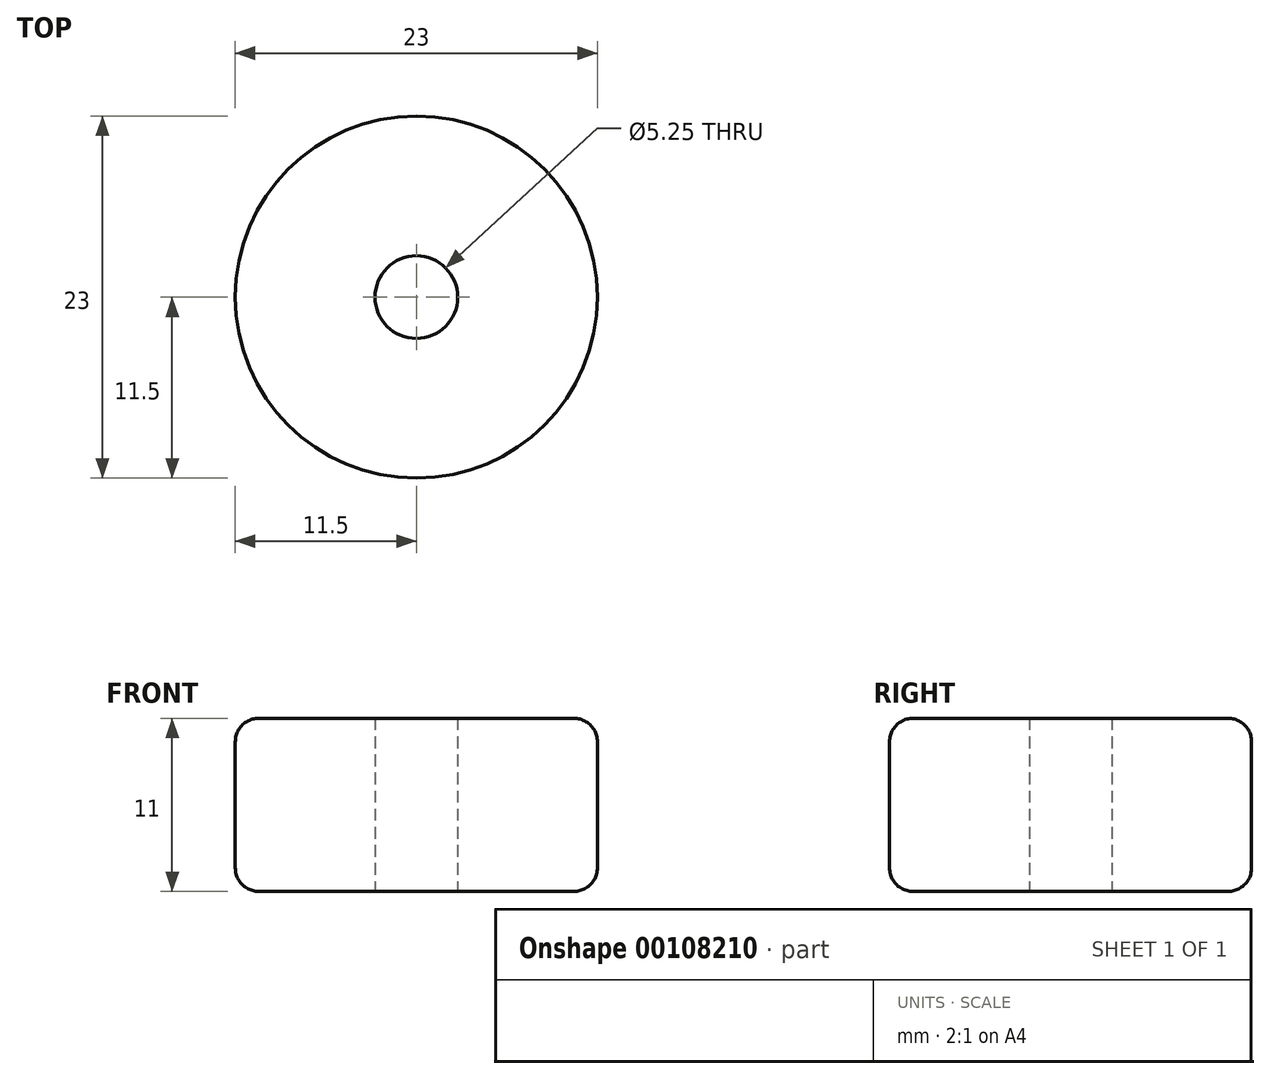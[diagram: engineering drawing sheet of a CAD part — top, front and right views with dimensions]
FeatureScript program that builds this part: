
annotation { "Feature Type Name" : "Feature", "Feature Type Description" : "" }
export const myFeature = defineFeature(function(context is Context, id is Id, definition is map)
    precondition{}
    {
        {
            var Q0;
            Q0=qCreatedBy(makeId("Top.planeOp"),FACE);
            var sketch = newSketch(context, id + "F0", { "sketchPlane" : qUnion([Q0])});
            skCircle(sketch, "E0", {"center": v(0, 0) * mm, "radius": 2.63 * mm});
            skCircle(sketch, "E1", {"center": v(0, 0) * mm, "radius": 11.5 * mm});
            skSolve(sketch);
        }
        {
            var Q0;
            Q0 = qSketchRegion(id + "F0", true);
            var Q1;
            Q1=makeQuery(id+"F0.imprint","IMPRINT",FACE,{"disambiguationData":[TD([[makeQuery(id+"F0.imprint","IMPRINT",EDGE,{"derivedFrom":sQuery(id+"F0.wireOp",EDGE,"E0")}),-1.0]])]});
            extrude(context, id + "F1", {"entities" : qUnion([Q0, Q1]), "depth" : 11 * mm});
        }
        {
            var Q0;
            Q0=makeQuery(id+"F1.opExtrude","CAP_EDGE",EDGE,{"disambiguationData":[OSD([sQuery(id+"F0.wireOp",EDGE,"E1")])],"isStart":false});
            var Q1;
            Q1=makeQuery(id+"F1.opExtrude","CAP_EDGE",EDGE,{"disambiguationData":[OSD([sQuery(id+"F0.wireOp",EDGE,"E1")])],"isStart":true});
            fillet(context, id + "F2", {"entities" : qUnion([Q0, Q1]), "radius" : 1.5 * mm, "tangentPropagation" : true, "allowEdgeOverflow" : false});
        }
    });
